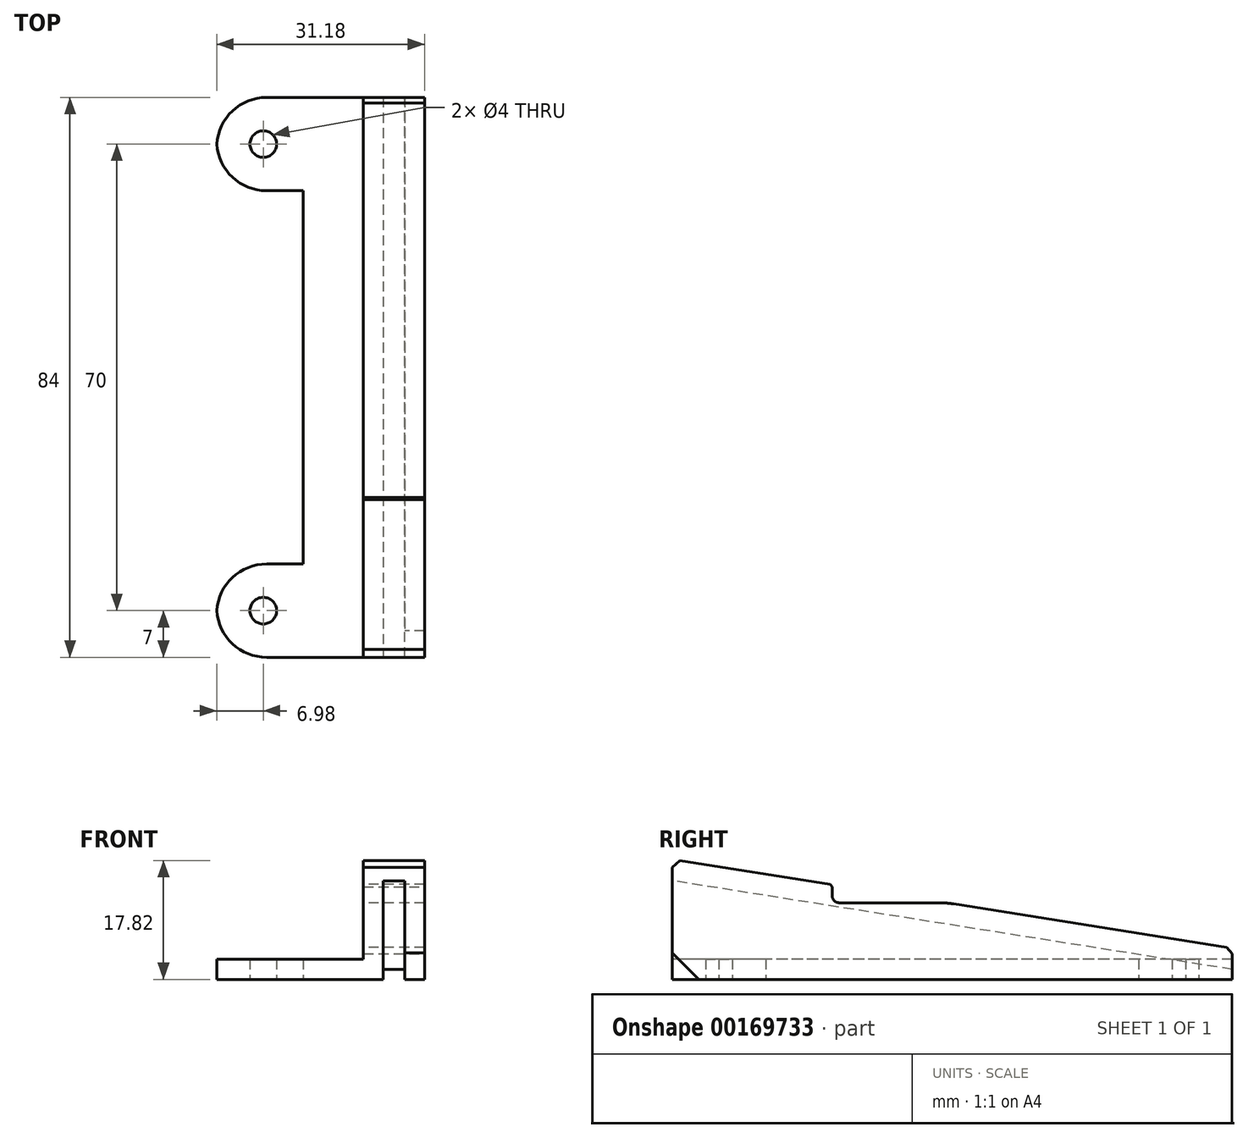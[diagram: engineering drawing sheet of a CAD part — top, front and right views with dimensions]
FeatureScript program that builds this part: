
annotation { "Feature Type Name" : "Feature", "Feature Type Description" : "" }
export const myFeature = defineFeature(function(context is Context, id is Id, definition is map)
    precondition{}
    {
        {
            var Q0;
            Q0=qCreatedBy(makeId("Top.planeOp"),FACE);
            var sketch = newSketch(context, id + "F0", { "sketchPlane" : qUnion([Q0])});
            skLineSegment(sketch, "E0", {"start": v(0, 0) * mm, "end": v(0, 84) * mm});
            skLineSegment(sketch, "E1", {"start": v(0, 84) * mm, "end": v(-25, 84) * mm});
            skLineSegment(sketch, "E2", {"start": v(-25, 84) * mm, "end": v(-25, 70) * mm});
            skLineSegment(sketch, "E3", {"start": v(-25, 70) * mm, "end": v(-12, 70) * mm});
            skLineSegment(sketch, "E4", {"start": v(-12, 70) * mm, "end": v(-12, 14) * mm});
            skLineSegment(sketch, "E5", {"start": v(-12, 14) * mm, "end": v(-25, 14) * mm});
            skLineSegment(sketch, "E6", {"start": v(-25, 14) * mm, "end": v(-25, 0) * mm});
            skLineSegment(sketch, "E7", {"start": v(-25, 0) * mm, "end": v(0, 0) * mm});
            skPoint(sketch, "E8", {"position": v(-25, 77) * mm});
            skPoint(sketch, "E9", {"position": v(-25, 7) * mm});
            skCircle(sketch, "E10", {"center": v(-18, 77) * mm, "radius": 2 * mm});
            skCircle(sketch, "E11", {"center": v(-18, 7) * mm, "radius": 2 * mm});
            skLineSegment(sketch, "E12", {"start": v(-3, 84) * mm, "end": v(-3, 0) * mm, "construction": true});
            skSolve(sketch);
        }
        {
            var Q0;
            Q0 = qSketchRegion(id + "F0", true);
            extrude(context, id + "F1", {"entities" : qUnion([Q0]), "depth" : 3 * mm});
        }
        {
            var Q0;
            Q0=qCreatedBy(makeId("Top.planeOp"),FACE);
            var sketch = newSketch(context, id + "F2", { "sketchPlane" : qUnion([Q0])});
            skLineSegment(sketch, "E13.bottom", {"start": v(3.2, 84) * mm, "end": v(6.2, 84) * mm});
            skLineSegment(sketch, "E13.top", {"start": v(3.2, 0) * mm, "end": v(6.2, 0) * mm});
            skLineSegment(sketch, "E13.left", {"start": v(3.2, 84) * mm, "end": v(3.2, 0) * mm});
            skLineSegment(sketch, "E13.right", {"start": v(6.2, 84) * mm, "end": v(6.2, 0) * mm});
            skLineSegment(sketch, "E14.bottom", {"start": v(0, 0) * mm, "end": v(-3, 0) * mm});
            skLineSegment(sketch, "E14.top", {"start": v(0, 84) * mm, "end": v(-3, 84) * mm});
            skLineSegment(sketch, "E14.left", {"start": v(0, 0) * mm, "end": v(0, 84) * mm});
            skLineSegment(sketch, "E14.right", {"start": v(-3, 0) * mm, "end": v(-3, 84) * mm});
            skSolve(sketch);
        }
        {
            var Q0;
            Q0 = qSketchRegion(id + "F2", true);
            extrude(context, id + "F3", {"entities" : qUnion([Q0]), "operationType" : NewBodyOperationType.ADD, "depth" : 18 * mm});
        }
        {
            var Q0;
            Q0=makeQuery(id+"F3.opExtrude","SWEPT_FACE",FACE,{"disambiguationData":[OSD([sQuery(id+"F2.wireOp",EDGE,"E13.right")])]});
            var sketch = newSketch(context, id + "F4", { "sketchPlane" : qUnion([Q0])});
            skLineSegment(sketch, "E15", {"start": v(0, 18) * mm, "end": v(84, 4.7) * mm});
            skLineSegment(sketch, "E16", {"start": v(84, 4.7) * mm, "end": v(84, 18) * mm});
            skLineSegment(sketch, "E17", {"start": v(84, 18) * mm, "end": v(0, 18) * mm});
            skSolve(sketch);
        }
        {
            var Q0;
            Q0 = qSketchRegion(id + "F4", true);
            var Q1;
            Q1=makeQuery(id+"F3.opExtrude","SWEPT_FACE",FACE,{"disambiguationData":[OSD([sQuery(id+"F2.wireOp",EDGE,"E14.right")])]});
            extrude(context, id + "F5", {"entities" : qUnion([Q0]), "operationType" : NewBodyOperationType.REMOVE, "endBound" : BoundingType.UP_TO_SURFACE, "oppositeDirection" : true, "endBoundEntityFace" : qUnion([Q1]), "depth" : 25 * mm});
        }
        {
            var Q0;
            Q0=makeQuery(id+"F3.opExtrude","SWEPT_FACE",FACE,{"disambiguationData":[OSD([sQuery(id+"F2.wireOp",EDGE,"E13.right")])]});
            var sketch = newSketch(context, id + "F6", { "sketchPlane" : qUnion([Q0])});
            skLineSegment(sketch, "E18", {"start": v(0, 18) * mm, "end": v(0, 14.8) * mm});
            skLineSegment(sketch, "E19", {"start": v(0, 14.8) * mm, "end": v(84, 1.5) * mm});
            skLineSegment(sketch, "E20", {"start": v(84, 1.5) * mm, "end": v(84, 4.7) * mm});
            skLineSegment(sketch, "E21", {"start": v(84, 4.7) * mm, "end": v(0, 18) * mm});
            skSolve(sketch);
        }
        {
            var Q0;
            Q0 = qSketchRegion(id + "F6", true);
            var Q1;
            Q1=makeQuery(id+"F3.opExtrude","SWEPT_FACE",FACE,{"disambiguationData":[OSD([sQuery(id+"F2.wireOp",EDGE,"E14.right")])]});
            extrude(context, id + "F7", {"entities" : qUnion([Q0]), "operationType" : NewBodyOperationType.ADD, "endBound" : BoundingType.UP_TO_SURFACE, "oppositeDirection" : true, "endBoundEntityFace" : qUnion([Q1]), "depth" : 25 * mm});
        }
        {
            var Q0;
            Q0=makeQuery(id+"F1.opExtrude","SWEPT_EDGE",EDGE,{"disambiguationData":[OSD([sQuery(id+"F0.wireOp",EDGE,"E2"),sQuery(id+"F0.wireOp",EDGE,"E3")])]});
            var Q1;
            Q1=makeQuery(id+"F1.opExtrude","SWEPT_EDGE",EDGE,{"disambiguationData":[OSD([sQuery(id+"F0.wireOp",EDGE,"E1"),sQuery(id+"F0.wireOp",EDGE,"E2")])]});
            var Q2;
            Q2=makeQuery(id+"F1.opExtrude","SWEPT_EDGE",EDGE,{"disambiguationData":[OSD([sQuery(id+"F0.wireOp",EDGE,"E6"),sQuery(id+"F0.wireOp",EDGE,"E7")])]});
            var Q3;
            Q3=makeQuery(id+"F1.opExtrude","SWEPT_EDGE",EDGE,{"disambiguationData":[OSD([sQuery(id+"F0.wireOp",EDGE,"E5"),sQuery(id+"F0.wireOp",EDGE,"E6")])]});
            fillet(context, id + "F8", {"entities" : qUnion([Q0, Q1, Q2, Q3]), "radius" : 7.5 * mm, "tangentPropagation" : true, "allowEdgeOverflow" : false});
        }
        {
            var Q0;
            Q0=makeQuery(id+"F3.opExtrude","SWEPT_FACE",FACE,{"disambiguationData":[OSD([sQuery(id+"F2.wireOp",EDGE,"E14.right")])]});
            var sketch = newSketch(context, id + "F9", { "sketchPlane" : qUnion([Q0])});
            skLineSegment(sketch, "E22.bottom", {"start": v(-24, 11.5) * mm, "end": v(-52, 11.5) * mm});
            skLineSegment(sketch, "E22.top", {"start": v(-24, 16.5) * mm, "end": v(-52, 16.5) * mm});
            skLineSegment(sketch, "E22.left", {"start": v(-24, 11.5) * mm, "end": v(-24, 16.5) * mm});
            skLineSegment(sketch, "E22.right", {"start": v(-52, 11.5) * mm, "end": v(-52, 16.5) * mm});
            skSolve(sketch);
        }
        {
            var Q0;
            Q0 = qSketchRegion(id + "F9", true);
            var Q1;
            Q1=makeQuery(id+"F3.opExtrude","SWEPT_FACE",FACE,{"disambiguationData":[OSD([sQuery(id+"F2.wireOp",EDGE,"E13.right")])]});
            extrude(context, id + "F10", {"entities" : qUnion([Q0]), "operationType" : NewBodyOperationType.REMOVE, "endBound" : BoundingType.UP_TO_SURFACE, "oppositeDirection" : true, "endBoundEntityFace" : qUnion([Q1]), "depth" : 25 * mm});
        }
        {
            var Q0;
            Q0=makeQuery(id+"F10.boolean.opBoolean","COPY",EDGE,{"derivedFrom":makeQuery(id+"F10.opExtrude","SWEPT_EDGE",EDGE,{"disambiguationData":[OSD([sQuery(id+"F9.wireOp",EDGE,"E22.bottom"),sQuery(id+"F9.wireOp",EDGE,"E22.left")])]})});
            fillet(context, id + "F11", {"entities" : qUnion([Q0]), "radius" : 1 * mm, "tangentPropagation" : true, "allowEdgeOverflow" : false});
        }
        {
            var Q0;
            {var subQ0=makeQuery(id+"F5.opExtrude","SWEPT_FACE",FACE,{"disambiguationData":[OSD([sQuery(id+"F4.wireOp",EDGE,"E15")])]});Q0=makeQuery(id+"F10.boolean.opBoolean","INTERSECT",EDGE,{"derivedFrom":[makeQuery(id+"F7.boolean.opBoolean","MERGE",FACE,{"derivedFrom":[makeQuery(id+"F5.boolean.opBoolean","COPY",FACE,{"disambiguationData":[TD([makeQuery(id+"F3.opExtrude","SWEPT_FACE",FACE,{"disambiguationData":[OSD([sQuery(id+"F2.wireOp",EDGE,"E13.bottom")])]})])],"derivedFrom":subQ0}),makeQuery(id+"F5.boolean.opBoolean","COPY",FACE,{"disambiguationData":[TD([makeQuery(id+"F1.opExtrude","SWEPT_FACE",FACE,{"disambiguationData":[OSD([sQuery(id+"F0.wireOp",EDGE,"E0")])]})])],"derivedFrom":subQ0}),makeQuery(id+"F7.opExtrude","SWEPT_FACE",FACE,{"disambiguationData":[OSD([sQuery(id+"F6.wireOp",EDGE,"E21")])]})]}),makeQuery(id+"F10.opExtrude","SWEPT_FACE",FACE,{"disambiguationData":[OSD([sQuery(id+"F9.wireOp",EDGE,"E22.bottom")])]})]});}
            fillet(context, id + "F12", {"entities" : qUnion([Q0]), "radius" : 15 * mm, "tangentPropagation" : true, "allowEdgeOverflow" : false});
        }
        {
            var Q0;
            {var subQ0=makeQuery(id+"F5.opExtrude","SWEPT_FACE",FACE,{"disambiguationData":[OSD([sQuery(id+"F4.wireOp",EDGE,"E15")])]});Q0=makeQuery(id+"F10.boolean.opBoolean","INTERSECT",EDGE,{"derivedFrom":[makeQuery(id+"F7.boolean.opBoolean","MERGE",FACE,{"derivedFrom":[makeQuery(id+"F5.boolean.opBoolean","COPY",FACE,{"disambiguationData":[TD([makeQuery(id+"F3.opExtrude","SWEPT_FACE",FACE,{"disambiguationData":[OSD([sQuery(id+"F2.wireOp",EDGE,"E13.bottom")])]})])],"derivedFrom":subQ0}),makeQuery(id+"F5.boolean.opBoolean","COPY",FACE,{"disambiguationData":[TD([makeQuery(id+"F1.opExtrude","SWEPT_FACE",FACE,{"disambiguationData":[OSD([sQuery(id+"F0.wireOp",EDGE,"E0")])]})])],"derivedFrom":subQ0}),makeQuery(id+"F7.opExtrude","SWEPT_FACE",FACE,{"disambiguationData":[OSD([sQuery(id+"F6.wireOp",EDGE,"E21")])]})]}),makeQuery(id+"F10.opExtrude","SWEPT_FACE",FACE,{"disambiguationData":[OSD([sQuery(id+"F9.wireOp",EDGE,"E22.left")])]})]});}
            chamfer(context, id + "F13", {"entities" : qUnion([Q0]), "width" : 0.4 * mm, "tangentPropagation" : true});
        }
        {
            var Q0;
            Q0=makeQuery(id+"F3.opExtrude","CAP_EDGE",EDGE,{"disambiguationData":[OSD([sQuery(id+"F2.wireOp",EDGE,"E13.top")])],"isStart":true});
            chamfer(context, id + "F14", {"entities" : qUnion([Q0]), "width" : 4 * mm, "tangentPropagation" : true});
        }
        {
            var Q0;
            {var subQ0=sQuery(id+"F2.wireOp",EDGE,"E13.top");var subQ1=makeQuery(id+"F5.opExtrude","SWEPT_EDGE",EDGE,{"disambiguationData":[OSD([subQ0,sQuery(id+"F2.wireOp",EDGE,"E13.right"),sQuery(id+"F4.wireOp",EDGE,"E15"),sQuery(id+"F4.wireOp",EDGE,"E17")])]});Q0=makeQuery(id+"F7.boolean.opBoolean","MERGE",EDGE,{"derivedFrom":[makeQuery(id+"F5.boolean.opBoolean","MERGE",EDGE,{"derivedFrom":[makeQuery(id+"F3.opExtrude","CAP_EDGE",EDGE,{"disambiguationData":[OSD([subQ0])],"isStart":false}),subQ1]}),makeQuery(id+"F5.boolean.opBoolean","MERGE",EDGE,{"derivedFrom":[makeQuery(id+"F3.opExtrude","CAP_EDGE",EDGE,{"disambiguationData":[OSD([sQuery(id+"F2.wireOp",EDGE,"E14.bottom")])],"isStart":false}),subQ1]}),makeQuery(id+"F7.opExtrude","SWEPT_EDGE",EDGE,{"disambiguationData":[OSD([sQuery(id+"F6.wireOp",EDGE,"E18"),sQuery(id+"F6.wireOp",EDGE,"E21")])]})]});}
            var Q1;
            {var subQ0=sQuery(id+"F2.wireOp",EDGE,"E13.bottom");var subQ1=sQuery(id+"F2.wireOp",EDGE,"E13.right");var subQ2=sQuery(id+"F4.wireOp",EDGE,"E15");var subQ4=makeQuery(id+"F5.opExtrude","SWEPT_EDGE",EDGE,{"disambiguationData":[OSD([subQ0,subQ1,subQ2,sQuery(id+"F4.wireOp",EDGE,"E16")])]});Q1=makeQuery(id+"F7.boolean.opBoolean","MERGE",EDGE,{"derivedFrom":[makeQuery(id+"F5.boolean.opBoolean","COPY",EDGE,{"disambiguationData":[TD([makeQuery(id+"F1.opExtrude","SWEPT_FACE",FACE,{"disambiguationData":[OSD([sQuery(id+"F0.wireOp",EDGE,"E0")])]})])],"derivedFrom":subQ4}),makeQuery(id+"F5.boolean.opBoolean","COPY",EDGE,{"disambiguationData":[TD([makeQuery(id+"F3.opExtrude","SWEPT_FACE",FACE,{"disambiguationData":[OSD([subQ0])]})])],"derivedFrom":subQ4}),makeQuery(id+"F7.opExtrude","SWEPT_EDGE",EDGE,{"disambiguationData":[OSD([sQuery(id+"F6.wireOp",EDGE,"E20"),sQuery(id+"F6.wireOp",EDGE,"E21")])]})]});}
            chamfer(context, id + "F15", {"entities" : qUnion([Q0, Q1]), "width" : 1 * mm, "tangentPropagation" : true});
        }
    });
